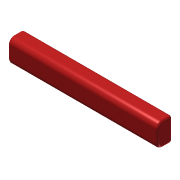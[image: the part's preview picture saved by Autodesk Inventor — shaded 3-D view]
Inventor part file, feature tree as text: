
AUTODESK INVENTOR PART (.ipt)
format: ipt  version: 2013 (Build 170138000, 138)  size: 123,392 bytes
history: native  units: in
note: dims shown in document units (in); Inventor stores cm internally (conversion verified against a paired STEP export)
features: extrude x3, sketch x3, projected_geometry x2, fillet x1
ambient origin geometry x8: Origin, YZ Plane, XZ Plane, XY Plane, X Axis, Y Axis, Z Axis, Center Point
bodies: Solid1 (feature_tree)
feature tree (9):
  extrude  "Extrusion1"  Depth=5.0in
  extrude  "Extrusion2"  Depth=2.5in
  extrude  "Extrusion4"  Depth=31.8in TaperAngle=0.0deg
  fillet  "Fillet1"  Radius=31.8in
  sketch  "Sketch1"  dims[d0=31.8in d1=5.0in]
  sketch  "Sketch2"  dims[d2=0.75in d3=0.0in d4=2.5in]
  sketch  "Sketch4"  dims[d5=2.5in d6=31.8in d7=0.0in d10=31.8in d11=0.0in d12=0.5in]
  projected_geometry  "Project Cut Edges1"
  projected_geometry  "Project Cut Edges2"
